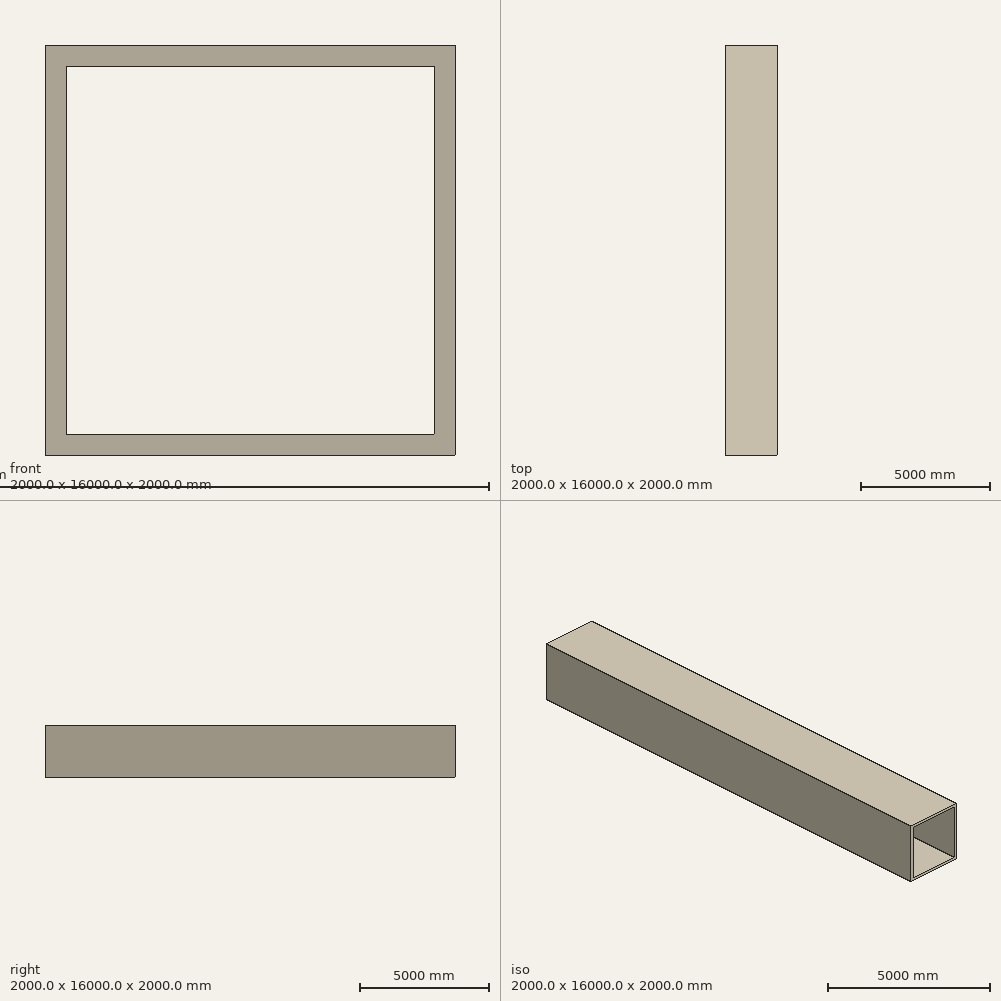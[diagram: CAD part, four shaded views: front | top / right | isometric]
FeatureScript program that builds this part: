
annotation { "Feature Type Name" : "Feature", "Feature Type Description" : "" }
export const myFeature = defineFeature(function(context is Context, id is Id, definition is map)
    precondition{}
    {
        {
            var Q0;
            Q0=qCreatedBy(makeId("Front.planeOp"),FACE);
            var sketch = newSketch(context, id + "F0", { "sketchPlane" : qUnion([Q0])});
            skLineSegment(sketch, "E0.bottom", {"start": v(0, 0) * mm, "end": v(2000, 0) * mm});
            skLineSegment(sketch, "E0.top", {"start": v(0, 2000) * mm, "end": v(2000, 2000) * mm});
            skLineSegment(sketch, "E0.left", {"start": v(0, 0) * mm, "end": v(0, 2000) * mm});
            skLineSegment(sketch, "E0.right", {"start": v(2000, 0) * mm, "end": v(2000, 2000) * mm});
            skLineSegment(sketch, "E1.bottom", {"start": v(100, 100) * mm, "end": v(1900, 100) * mm});
            skLineSegment(sketch, "E1.top", {"start": v(100, 1900) * mm, "end": v(1900, 1900) * mm});
            skLineSegment(sketch, "E1.left", {"start": v(100, 100) * mm, "end": v(100, 1900) * mm});
            skLineSegment(sketch, "E1.right", {"start": v(1900, 100) * mm, "end": v(1900, 1900) * mm});
            skSolve(sketch);
        }
        {
            var Q0;
            Q0=makeQuery(id+"F0.imprint","IMPRINT",FACE,{"disambiguationData":[TD([[makeQuery(id+"F0.imprint","IMPRINT",EDGE,{"derivedFrom":sQuery(id+"F0.wireOp",EDGE,"E0.bottom")}),1.0]])]});
            extrude(context, id + "F1", {"entities" : qUnion([Q0]), "depth" : 16000 * mm, "offsetDistance" : 25 * mm});
        }
    });
